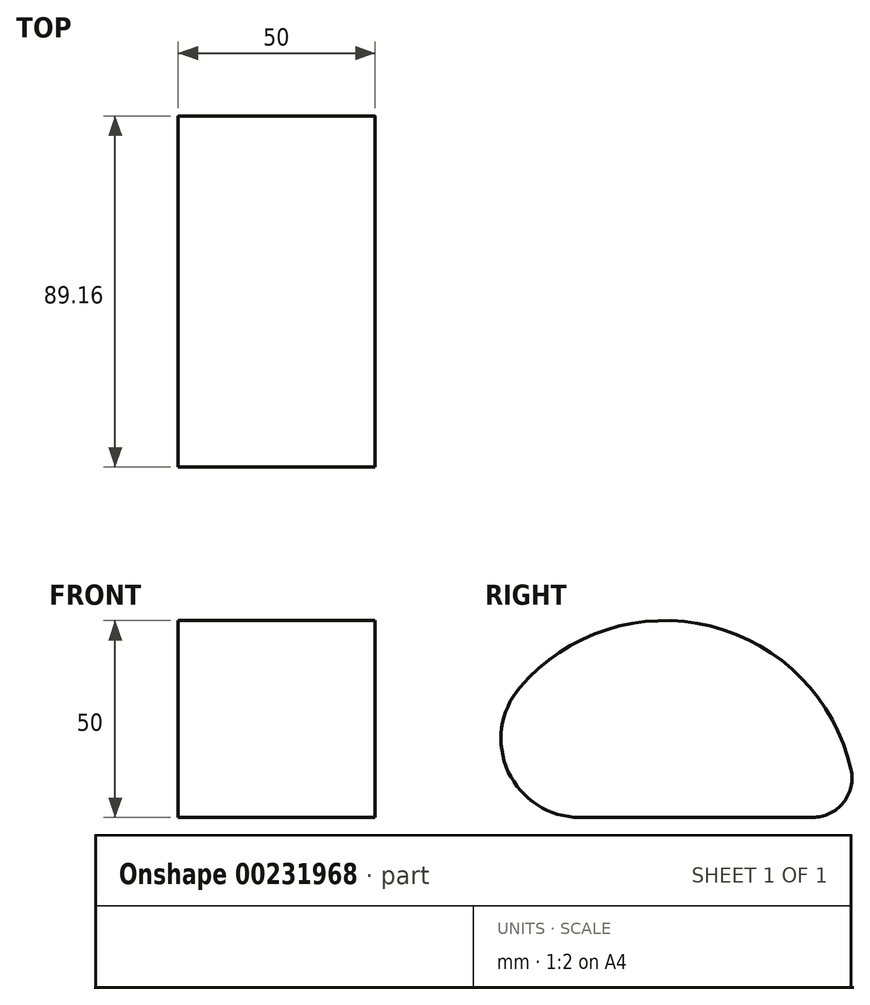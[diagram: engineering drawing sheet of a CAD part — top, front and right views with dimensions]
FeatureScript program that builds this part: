
annotation { "Feature Type Name" : "Feature", "Feature Type Description" : "" }
export const myFeature = defineFeature(function(context is Context, id is Id, definition is map)
    precondition{}
    {
        {
            var Q0;
            Q0=qCreatedBy(makeId("Right.planeOp"),FACE);
            var sketch = newSketch(context, id + "F0", { "sketchPlane" : qUnion([Q0])});
            skLineSegment(sketch, "E0", {"start": v(-53.94, 17.65) * mm, "end": v(5.22, 17.65) * mm});
            skArc(sketch, "E1", {"start": v(-53.94, 17.65) * mm, "mid": v(-72.1, 29.26) * mm, "end": v(-69.17, 50.62) * mm});
            skArc(sketch, "E2", {"start": v(-69.17, 50.62) * mm, "mid": v(-20.68, 66.23) * mm, "end": v(14.97, 29.84) * mm});
            skArc(sketch, "E3", {"start": v(14.97, 29.84) * mm, "mid": v(13.03, 21.4) * mm, "end": v(5.22, 17.65) * mm});
            skSolve(sketch);
        }
        {
            var Q0;
            Q0 = qSketchRegion(id + "F0", true);
            extrude(context, id + "F1", {"entities" : qUnion([Q0]), "oppositeDirection" : true, "depth" : 50 * mm});
        }
    });
